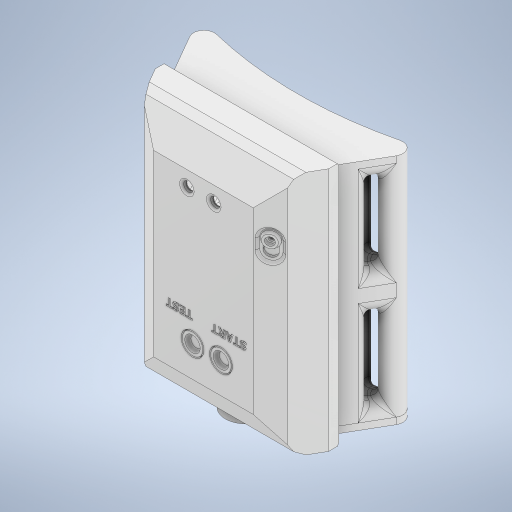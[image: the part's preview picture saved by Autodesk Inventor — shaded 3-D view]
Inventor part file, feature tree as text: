
AUTODESK INVENTOR PART (.ipt)
format: ipt  version: 2024.3 (Build 283343000, 343)  size: 3,819,520 bytes
history: native  units: mm
features: extrude x46, projected_geometry x44, sketch x42, reference x16, fillet x15, other x11, plane x7, chamfer x6, thicken_offset x4, mirror x3, split x3, boolean_combine x2, shell x1
ambient origin geometry x8: Origin, YZ Plane, XZ Plane, XY Plane, X Axis, Y Axis, Z Axis, Center Point
bodies: Solid1 (feature_tree), Solid4 (feature_tree), Solid5 (feature_tree), Solid8 (feature_tree), Solid9 (feature_tree), Solid11 (feature_tree), Solid12 (feature_tree), Solid2 (feature_tree), Solid3 (feature_tree)
feature tree (200):
  extrude  "Extrusion1"  Depth=55.0mm
  extrude  "Extrusion2"  TaperAngle=0.0deg  [1 undecoded]
  extrude  "Extrusion3"  TaperAngle=0.0deg  [1 undecoded]
  fillet  "Fillet1"  Radius=4.0mm
  plane  "Work Plane1"
  extrude  "Extrusion4"  Depth=2.0mm TaperAngle=0.0deg
  fillet  "Fillet2"  Radius=2.0mm
  fillet  "Fillet3"  Radius=5.0mm
  fillet  "Fillet4"  Radius=2.0mm
  mirror  "Mirror1"
  split  "Split1"
  mirror  "Mirror2"
  extrude  "Extrusion5"  Depth=3.0mm
  shell  "Shell1"  Thickness=2.0mm
  plane  "Work Plane2"
  extrude  "Extrusion6"  Depth=2.0mm
  chamfer  "Chamfer1"  Distance=30.0mm
  plane  "Work Plane3"
  extrude  "Extrusion7"  TaperAngle=0.0deg  [1 undecoded]
  extrude  "Extrusion8"  Depth=0.5mm TaperAngle=45.0deg
  split  "Split2"
  extrude  "Extrusion9"  Depth=1.0mm TaperAngle=0.0deg
  extrude  "Extrusion10"  TaperAngle=45.0deg  [1 undecoded]
  mirror  "Mirror3"
  plane  "Work Plane4"
  split  "Split3"
  extrude  "Extrusion11"  Depth=3.0mm TaperAngle=0.0deg
  fillet  "Fillet5"  Radius=2.0mm
  fillet  "Fillet6"  Radius=3.0mm
  extrude  "Extrusion12"  Depth=4.0mm
  extrude  "Extrusion13"  Depth=1.0mm
  thicken_offset  "Thicken1"
  thicken_offset  "Thicken2"
  extrude  "Extrusion14"  Depth=1.0mm
  boolean_combine  "Combine1"
  boolean_combine  "Combine2"
  extrude  "Extrusion15"  Depth=0.5mm
  fillet  "Fillet7"  Radius=0.5mm
  extrude  "Extrusion16"  Depth=2.0mm
  extrude  "Extrusion17"  Depth=1.0mm
  fillet  "Fillet8"  Radius=15.0mm
  sketch  "Sketch18"  dims[d62=2.4mm d63=2.0mm]
  extrude  "Extrusion18"  Depth=2.0mm
  extrude  "Extrusion19"  Depth=2.0mm
  fillet  "Fillet9"  Radius=4.0mm
  extrude  "Extrusion20"  Depth=1.0mm
  thicken_offset  "Thicken3"
  thicken_offset  "Thicken4"
  plane  "Work Plane5"
  extrude  "Extrusion21"  Depth=4.0mm TaperAngle=0.0deg
  chamfer  "Chamfer2"  Distance=10.0mm
  chamfer  "Chamfer3"  Distance=4.0mm
  extrude  "Extrusion22"  Depth=4.0mm TaperAngle=0.0deg
  fillet  "Fillet10"  Radius=10.0mm
  extrude  "Extrusion28"  Depth=0.3mm
  sketch  "Sketch28"  dims[d76=0.7mm]
  extrude  "Extrusion29"  Depth=0.3mm
  extrude  "Extrusion30"  Depth=8.0mm
  extrude  "Extrusion31"  Depth=0.5mm
  extrude  "Extrusion32"  Depth=0.5mm
  fillet  "Fillet11"  Radius=0.5mm
  fillet  "Fillet12"  Radius=0.5mm
  extrude  "Extrusion33"  Depth=2.0mm
  extrude  "Extrusion34"  Depth=2.0mm
  plane  "Work Plane7"
  extrude  "Extrusion35"  Depth=2.0mm TaperAngle=0.0deg
  extrude  "Extrusion36"  Depth=2.0mm
  extrude  "Extrusion37"  Depth=1.0mm
  extrude  "Extrusion38"  Depth=1.0mm
  extrude  "Extrusion39"  Depth=1.0mm
  extrude  "Extrusion40"  Depth=1.0mm
  chamfer  "Chamfer4"  Distance=0.3mm
  chamfer  "Chamfer5"  Distance=4.0mm
  fillet  "Fillet13"  Radius=1.5mm
  sketch  "Sketch38"  dims[d97=1.5mm d98=0.3mm]
  extrude  "Extrusion41"  Depth=4.0mm
  extrude  "Extrusion42"  Depth=2.0mm TaperAngle=0.0deg
  sketch  "Sketch39"  dims[d99=5.0mm d100=0.3mm]
  extrude  "Extrusion43"  Depth=1.0mm TaperAngle=30.0deg
  chamfer  "Chamfer6"  Distance=14.2mm Angle=30.0deg
  extrude  "Extrusion44"  Depth=1.0mm
  plane  "Work Plane8"
  extrude  "Extrusion45"  Depth=3.0mm TaperAngle=0.0deg
  fillet  "Fillet14"  Radius=2.0mm
  extrude  "Extrusion46"  Depth=1.0mm
  extrude  "Extrusion47"  Depth=1.0mm
  extrude  "Extrusion48"  TaperAngle=150.0deg  [1 undecoded]
  extrude  "Extrusion49"  Depth=1.0mm
  extrude  "Extrusion50"  Depth=1.0mm
  extrude  "Extrusion51"  Depth=1.0mm
  fillet  "Fillet15"  Radius=2.0mm
  sketch  "Sketch1"  dims[d0=30.0mm d1=30.0deg d2=55.0mm]
  sketch  "Sketch2"  dims[d3=90.0mm d4=0.0mm d5=0.0mm]
  sketch  "Sketch3"  dims[d6=150.0mm d7=0.0mm d8=0.0mm d9=4.0mm]
  sketch  "Sketch4"  dims[d10=5.0mm d11=30.0mm d12=0.0mm d13=2.0mm d14=5.0mm d15=2.0mm]
  sketch  "Sketch5"  dims[d16=1.5mm d17=3.0mm d18=2.0mm]
  sketch  "Sketch6"  dims[d19=2.0mm d20=30.0mm d22=1.22173mm d24=30.0mm d26=1.22173mm]
  reference  "Reference1"
  sketch  "Sketch7"  dims[d28=0.0mm d29=0.0mm d30=0.0mm d31=0.0mm]
  projected_geometry  "Projected Loop1"
  reference  "Reference2"
  sketch  "Sketch8"  dims[d32=0.2mm d33=0.5mm d34=1.5mm d35=45.0deg]
  projected_geometry  "Projected Loop2"
  sketch  "Sketch9"  dims[d36=2.0mm d37=1.0mm d38=0.0mm]
  projected_geometry  "Projected Loop3"
  sketch  "Sketch10"  dims[d39=1.0mm d40=0.0mm d41=45.0deg]
  projected_geometry  "Projected Loop4"
  sketch  "Sketch11"  dims[d42=20.361989mm d43=15.0mm d44=0.0mm d45=2.0mm d46=3.0mm]
  projected_geometry  "Projected Loop5"
  sketch  "Sketch12"  dims[d47=3.0mm d48=4.0mm]
  projected_geometry  "Projected Loop6"
  projected_geometry  "Projected Loop7"
  sketch  "Sketch13"  dims[d49=4.0mm d50=1.0mm]
  sketch  "Sketch14"  dims[d51=1.0mm d52=1.0mm]
  projected_geometry  "Projected Loop8"
  projected_geometry  "Projected Loop9"
  projected_geometry  "Projected Loop10"
  sketch  "Sketch15"  dims[d53=60.0deg d54=0.5mm d55=0.5mm]
  reference  "Reference3"
  sketch  "Sketch16"  dims[d56=1.8mm d57=2.0mm]
  projected_geometry  "Projected Loop11"
  reference  "Reference4"
  sketch  "Sketch17"  dims[d58=1.2mm d59=1.0mm d60=15.0mm d61=0.0mm]
  projected_geometry  "Projected Loop12"
  projected_geometry  "Projected Loop13"
  sketch  "Sketch19"  dims[d64=5.0mm d65=2.0mm d66=4.0mm d67=0.0mm]
  projected_geometry  "Projected Loop14"
  projected_geometry  "Projected Loop15"
  sketch  "Sketch20"  dims[d68=1.0mm d69=6.1mm]
  reference  "Reference5"
  reference  "Reference6"
  sketch  "Sketch21"  dims[d70=1.5mm d71=4.0mm d72=0.0mm d73=10.0mm d74=0.0mm]
  projected_geometry  "Projected Loop16"
  sketch  "Sketch27"  dims[d75=0.7mm]
  reference  "Reference8"
  reference  "Reference9"
  sketch  "Sketch29"  dims[d77=0.7mm]
  reference  "Reference10"
  reference  "Reference11"
  sketch  "Sketch30"  dims[d78=0.7mm]
  reference  "Reference12"
  reference  "Reference13"
  reference  "Reference14"
  projected_geometry  "Projected Loop25"
  projected_geometry  "Projected Loop26"
  sketch  "Sketch31"  dims[d79=0.25mm]
  projected_geometry  "Projected Loop27"
  sketch  "Sketch32"  dims[d80=0.25mm]
  reference  "Reference15"
  sketch  "Sketch33"  dims[d84=1.5mm]
  projected_geometry  "Projected Loop28"
  sketch  "Sketch34"  dims[d85=1.5mm]
  projected_geometry  "Projected Loop29"
  sketch  "Sketch35"  dims[d86=1.5mm]
  projected_geometry  "Projected Loop30"
  sketch  "Sketch36"  dims[d87=1.5mm d88=4.0mm d89=0.0mm]
  sketch  "Sketch37"  dims[d90=0.25mm d91=4.0mm d92=0.0mm d95=10.0mm d96=0.0mm]
  projected_geometry  "Projected Loop31"
  projected_geometry  "Projected Loop32"
  projected_geometry  "Projected Loop33"
  projected_geometry  "Projected Loop34"
  projected_geometry  "Projected Loop35"
  sketch  "Sketch40"  dims[d101=1.5mm d102=8.0mm]
  reference  "Reference16"
  reference  "Reference17"
  sketch  "Sketch41"  dims[d103=1.2mm d104=0.5mm]
  sketch  "Sketch42"  dims[d105=0.5mm d106=0.5mm d107=0.5mm d108=0.5mm d109=0.0mm]
  projected_geometry  "Projected Loop36"
  sketch  "Sketch43"  dims[d110=0.5mm d111=2.0mm]
  sketch  "Sketch44"  dims[d112=0.3mm d113=2.0mm]
  projected_geometry  "Projected Loop37"
  sketch  "Sketch45"  dims[d114=2.0mm d115=0.0mm d116=2.0mm d117=0.0mm]
  projected_geometry  "Projected Loop38"
  projected_geometry  "Projected Loop39"
  projected_geometry  "Projected Loop40"
  projected_geometry  "Projected Loop41"
  projected_geometry  "Projected Loop42"
  projected_geometry  "Projected Loop43"
  projected_geometry  "Projected Loop44"
  sketch  "Sketch46"  dims[d118=1.0mm d119=2.0mm]
  sketch  "Sketch47"  dims[d120=10.0mm d121=0.0mm d122=0.2mm d123=0.2mm d124=0.2mm d125=0.2mm d126=0.3mm d127=4.0mm d128=1.5mm d129=4.0mm d130=2.0mm d131=0.0mm d132=14.2mm d133=13.25mm d134=30.0deg d135=14.2mm d136=13.25mm d137=30.0deg d138=1.5mm d139=3.0mm d140=0.0mm d141=2.0mm d159=0.5mm d160=0.3mm d163=150.0deg d164=1.5mm d166=5.0mm d167=5.0mm d168=2.0mm d169=106.0mm d170=0.0mm d171=0.3mm d175=60.0deg d176=2.0mm d177=2.7mm d178=120.0deg d179=0.0mm d180=0.0mm d181=10.0mm d182=0.0mm d183=10.0mm d184=0.0mm d185=5.0mm d186=0.3mm d187=0.3mm d190=2.0mm d191=0.3mm d192=0.3mm d193=10.0mm d194=3.490659mm d195=1.0mm d196=0.5mm d197=2.0mm d198=2.0mm d199=2.0mm d200=2.0mm d201=2.0mm d202=2.0mm d203=2.0mm d204=2.0mm d205=2.0mm d206=4.0mm d207=0.0mm d208=0.0mm d209=2.0mm d210=1.0mm d211=-7.853982mm d212=-8.5mm d213=0.3mm d215=1.5mm d216=3.2mm d217=0.0mm d218=1.5mm d219=0.0mm d220=0.3mm d221=0.5mm d222=0.0mm d223=1.0mm d224=-5.235988mm d225=4.060254mm d226=1.0mm d227=0.0mm d228=0.5mm d229=1.0mm d230=0.0mm d231=4.13mm d232=1.36mm d233=30.0deg d234=4.1mm d235=2.94mm d236=30.0deg d237=3.0mm d238=2.0mm d239=3.2mm d240=5.5mm d241=-0.349066mm d242=1.5mm d243=0.0mm d244=0.3mm d245=0.3mm d247=60.0deg d248=0.5mm d249=0.5mm d250=6.0mm d251=0.0mm d252=2.0mm d253=6.0mm d254=30.0deg d255=0.4mm d256=0.4mm d257=0.0mm d258=0.0mm d259=60.0deg d260=60.0deg d261=4.0mm d262=1.5mm d263=1.5mm d264=1.5mm d265=0.0mm d266=1.0mm d267=1.0mm d268=1.0mm d269=1.5mm d270=-5.235988mm d271=0.4mm d272=0.0mm d273=6.0mm d274=0.0mm d275=0.3mm d276=0.3mm d277=5.0mm d278=0.3mm d279=0.3mm d280=5.0mm d281=2.0mm d282=0.3mm d283=30.0mm d284=2.0mm d285=3.0mm d286=0.0mm d287=3.0mm d288=0.0mm d289=5.0mm d290=1.0mm d291=4.0mm d292=2.0mm d293=0.0mm d294=1.0mm]
  projected_geometry  "Projected Loop45"
  projected_geometry  "Project Cut Edges1"
  projected_geometry  "Project Cut Edges2"
  projected_geometry  "Project Cut Edges3"
  other  "<userpath> TUF\Documents\Inventor\ParkinsonDetection\Prototy-1.iam"
  other  "Prototy-1.iam"
  other  "Pin:1"
  projected_geometry  "Project Cut Edges4"
  other  "Buzzer:1"
  projected_geometry  "Project Cut Edges5"
  other  "PCB-V1:1"
  projected_geometry  "Project Cut Edges7"
  other  "3296W:2"
  other  "Holder-PCB:1"
  other  "3296W:1"
  other  "Switch:1"
  other  "TACTILE SWITCH:1"
  other  "TACTILE SWITCH:2"
  projected_geometry  "Project Cut Edges8"
note: 5 required parameter values undecoded (feature->parameter linkage not recoverable at this tier; creation-order binding heuristic only, values carry confidence <= 0.55)
